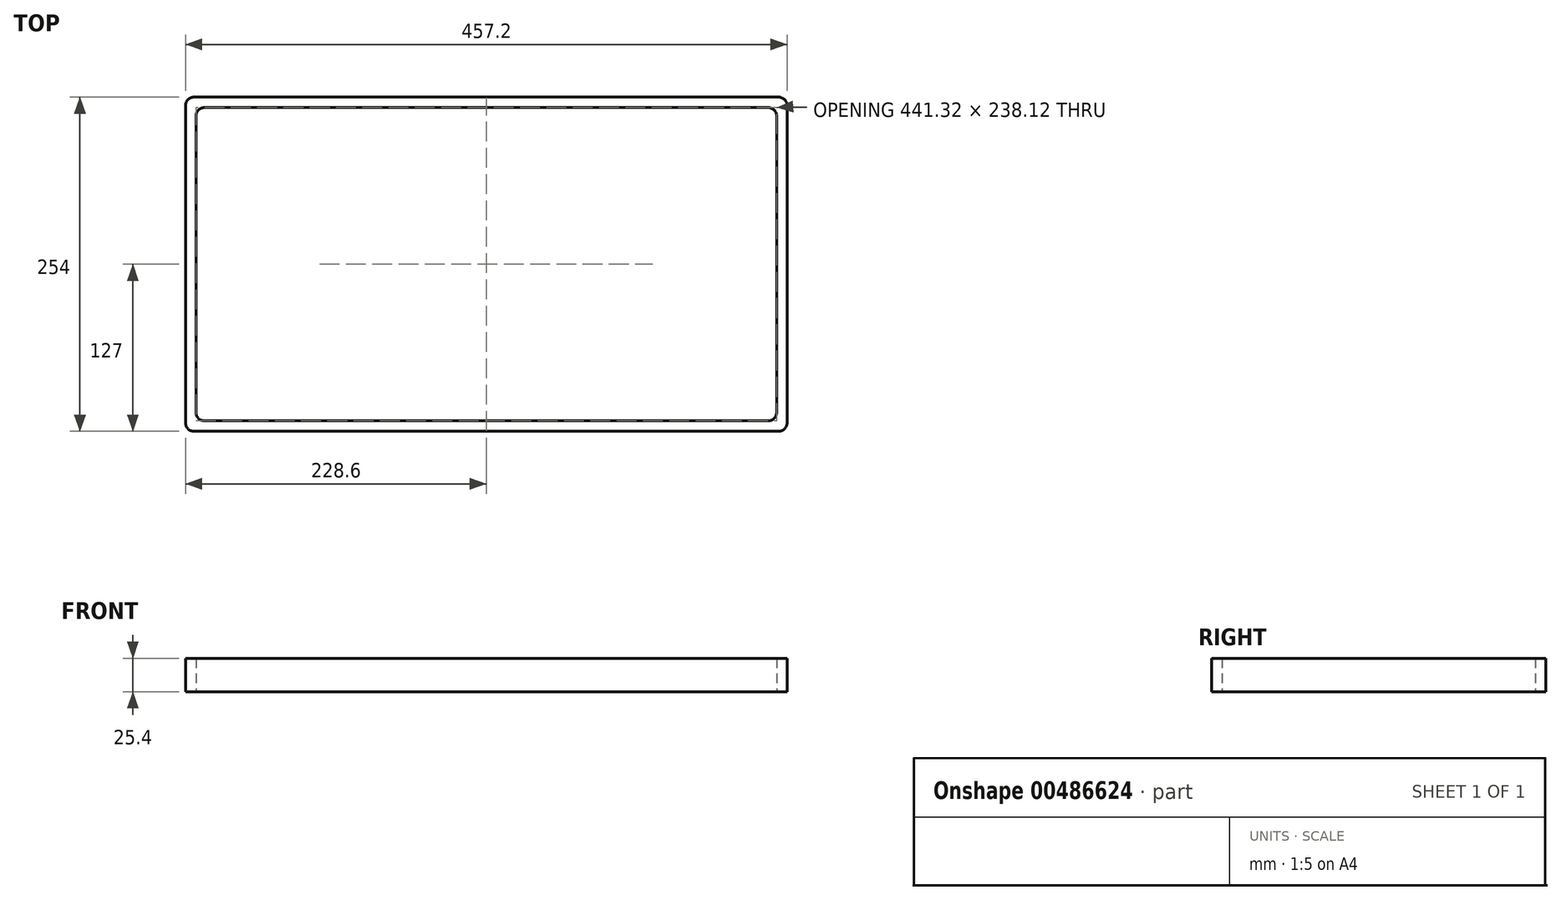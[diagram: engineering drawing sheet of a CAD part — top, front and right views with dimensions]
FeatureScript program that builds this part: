
annotation { "Feature Type Name" : "Feature", "Feature Type Description" : "" }
export const myFeature = defineFeature(function(context is Context, id is Id, definition is map)
    precondition{}
    {
        {
            var Q0;
            Q0=qCreatedBy(makeId("Top.planeOp"),FACE);
            var sketch = newSketch(context, id + "F0", { "sketchPlane" : qUnion([Q0])});
            skLineSegment(sketch, "E0.bottom", {"start": v(6.35, 0) * mm, "end": v(450.85, 0) * mm});
            skLineSegment(sketch, "E0.top", {"start": v(6.35, 254) * mm, "end": v(450.85, 254) * mm});
            skLineSegment(sketch, "E0.left", {"start": v(0, 6.35) * mm, "end": v(0, 247.65) * mm});
            skLineSegment(sketch, "E0.right", {"start": v(457.2, 6.35) * mm, "end": v(457.2, 247.65) * mm});
            skPoint(sketch, "E1.visualSharp", {"position": v(0, 254) * mm});
            skArc(sketch, "E1.filletArc", {"start": v(6.35, 254) * mm, "mid": v(1.86, 252.14) * mm, "end": v(0, 247.65) * mm});
            skPoint(sketch, "E2.visualSharp", {"position": v(457.2, 254) * mm});
            skArc(sketch, "E2.filletArc", {"start": v(457.2, 247.65) * mm, "mid": v(455.34, 252.14) * mm, "end": v(450.85, 254) * mm});
            skPoint(sketch, "E3.visualSharp", {"position": v(457.2, 0) * mm});
            skArc(sketch, "E3.filletArc", {"start": v(450.85, 0) * mm, "mid": v(455.34, 1.86) * mm, "end": v(457.2, 6.35) * mm});
            skPoint(sketch, "E4.visualSharp", {"position": v(0, 0) * mm});
            skArc(sketch, "E4.filletArc", {"start": v(0, 6.35) * mm, "mid": v(1.86, 1.86) * mm, "end": v(6.35, 0) * mm});
            skLineSegment(sketch, "E5.bottom", {"start": v(14.29, 7.94) * mm, "end": v(442.91, 7.94) * mm});
            skLineSegment(sketch, "E5.top", {"start": v(14.29, 246.06) * mm, "end": v(442.91, 246.06) * mm});
            skLineSegment(sketch, "E5.left", {"start": v(7.94, 14.29) * mm, "end": v(7.94, 239.71) * mm});
            skLineSegment(sketch, "E5.right", {"start": v(449.26, 14.29) * mm, "end": v(449.26, 239.71) * mm});
            skPoint(sketch, "E6.visualSharp", {"position": v(7.94, 246.06) * mm});
            skArc(sketch, "E6.filletArc", {"start": v(14.29, 246.06) * mm, "mid": v(9.8, 244.2) * mm, "end": v(7.94, 239.71) * mm});
            skPoint(sketch, "E7.visualSharp", {"position": v(7.94, 7.94) * mm});
            skArc(sketch, "E7.filletArc", {"start": v(7.94, 14.29) * mm, "mid": v(9.8, 9.8) * mm, "end": v(14.29, 7.94) * mm});
            skPoint(sketch, "E8.visualSharp", {"position": v(449.26, 7.94) * mm});
            skArc(sketch, "E8.filletArc", {"start": v(442.91, 7.94) * mm, "mid": v(447.4, 9.8) * mm, "end": v(449.26, 14.29) * mm});
            skPoint(sketch, "E9.visualSharp", {"position": v(449.26, 246.06) * mm});
            skArc(sketch, "E9.filletArc", {"start": v(449.26, 239.71) * mm, "mid": v(447.4, 244.2) * mm, "end": v(442.91, 246.06) * mm});
            skSolve(sketch);
        }
        {
            var Q0;
            Q0 = qSketchRegion(id + "F0", true);
            extrude(context, id + "F1", {"entities" : qUnion([Q0]), "depth" : 25.4 * mm});
        }
    });
